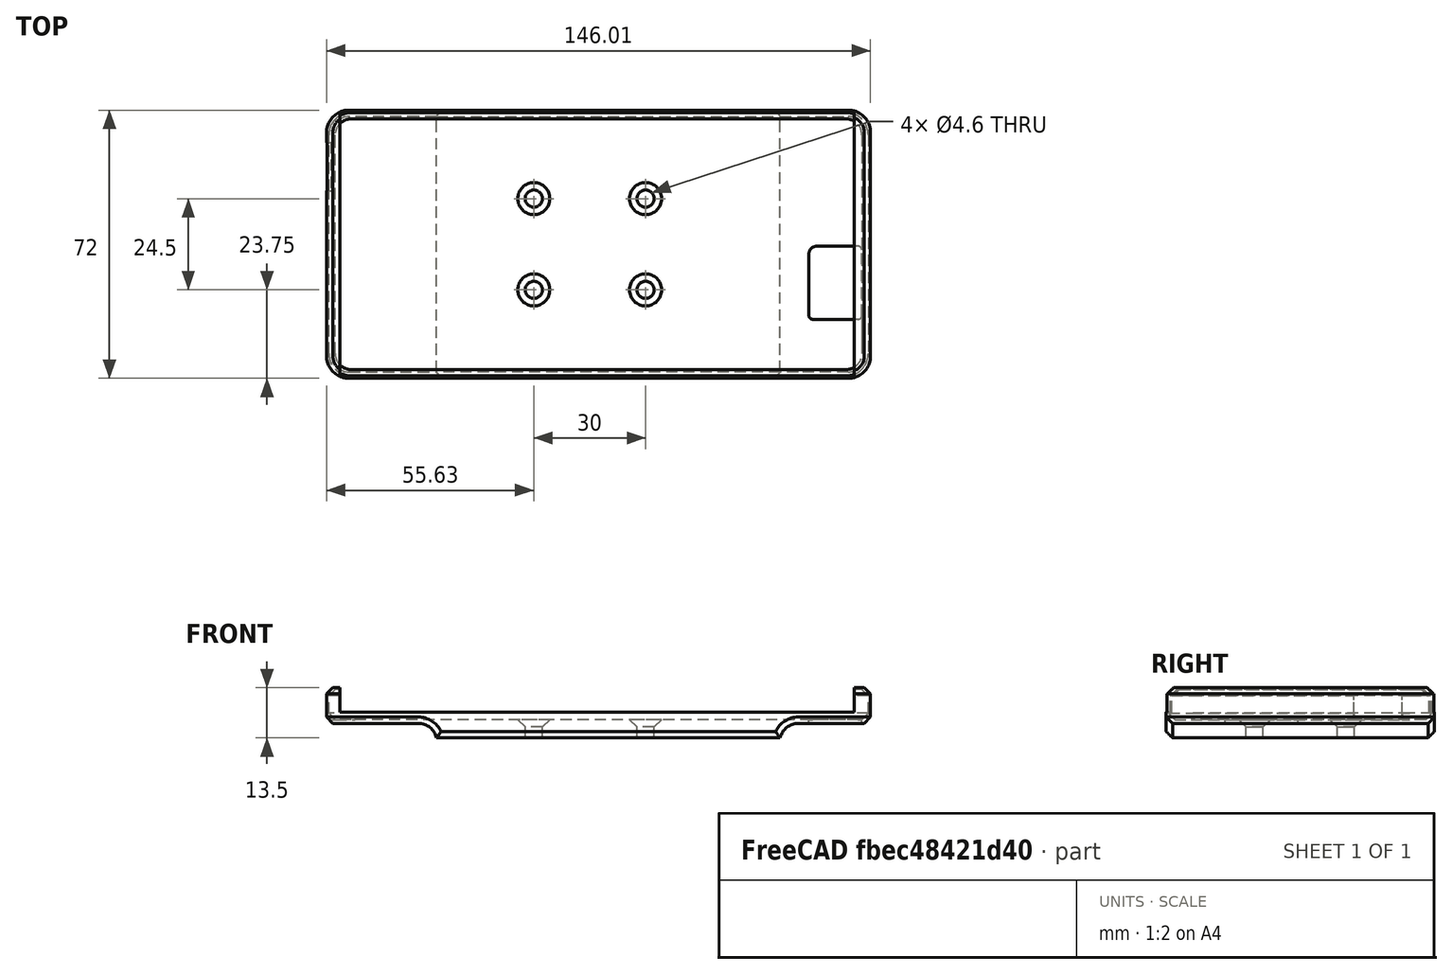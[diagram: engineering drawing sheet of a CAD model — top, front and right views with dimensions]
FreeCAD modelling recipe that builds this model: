
FCSTD DOCUMENT  (FreeCAD 0.16R5235 (Git))
Label: support_wiko_smart-roadster_i02
License: All rights reserved
LicenseURL: http://en.wikipedia.org/wiki/All_rights_reserved
objects: Part::Box×7, Part::Cut×7, Part::Fillet×5, Part::Chamfer×5, Part::Cylinder×4, Part::Fuse×3
note: 31 computed .brp shape members not serialized (recipe doc carries the construction recipe); baked Part::Feature solids carry a one-line shape summary decoded from their .brp

FEATURE [Part::Box] Box  label="Base_Highway_4G"
  Height = 8.1
  Length = 144.75
  Width = 70.7
FEATURE [Part::Box] Box001  label="Base_boitier"
  Height = 13.5
  Length = 146
  Placement = pos=(-0.625,-0.65,-4.9) rot=(0,0,1;0rad)
  Width = 72
FEATURE [Part::Fillet] Fillet  label="W_Rayon_6"
  Base = -> Box
  Edges = 4 edges r=6: [Edge1,Edge3,Edge5,Edge7]
FEATURE [Part::Fillet] Fillet001  label="B_Rayon_6"
  Base = -> Box001
  Edges = 4 edges r=6: [Edge1,Edge3,Edge5,Edge7]
FEATURE [Part::Chamfer] Chamfer  label="W_Chanf_1,7"
  Base = -> Fillet
  Edges = 2 edges r=1.7: [Edge1,Edge4]
FEATURE [Part::Cut] Cut  label="Boitier_trouée_wiko"
  Base = -> Fillet001
  Tool = -> Chamfer
FEATURE [Part::Box] Box002  label="Cube_trou_ouverture_supérieure"
  Height = 10
  Length = 138
  Placement = pos=(3,-4,2) rot=(0,0,1;0rad)
  Width = 80
FEATURE [Part::Cut] Cut001  label="Boitier_ouvert"
  Base = -> Cut
  Tool = -> Box002
FEATURE [Part::Chamfer] Chamfer001  label="Boitier_ouvert_chanf"
  Base = -> Cut001
  Edges = 3 edges r=1.7: [Edge1,Edge4,Edge48]
FEATURE [Part::Cylinder] Cylinder  label="Trou_fixation_1"
  Angle = 360
  Height = 15
  Placement = pos=(0,0,-7) rot=(0,0,1;0rad)
  Radius = 2.3
FEATURE [Part::Cylinder] Cylinder001  label="Trou_fixation_2"
  Angle = 360
  Height = 15
  Placement = pos=(0,24.5,-7) rot=(0,0,1;0rad)
  Radius = 2.3
FEATURE [Part::Cylinder] Cylinder002  label="Trou_fixation_3"
  Angle = 360
  Height = 15
  Placement = pos=(30,24.5,-7) rot=(0,0,1;0rad)
  Radius = 2.3
FEATURE [Part::Cylinder] Cylinder003  label="Trou_fixation_4"
  Angle = 360
  Height = 15
  Placement = pos=(30,0,-7) rot=(0,0,1;0rad)
  Radius = 2.3
FEATURE [Part::Fuse] Fusion
  Base = -> Cylinder
  Tool = -> Cylinder001
FEATURE [Part::Fuse] Fusion001
  Base = -> Fusion
  Tool = -> Cylinder002
FEATURE [Part::Fuse] Fusion002  label="Bloc_des_trous"
  Base = -> Fusion001
  Placement = pos=(55,23.1,0) rot=(0,0,1;0rad)
  Tool = -> Cylinder003
FEATURE [Part::Cut] Cut002  label="Boitier_percé_fix"
  Base = -> Chamfer001
  Tool = -> Fusion002
FEATURE [Part::Chamfer] Chamfer002  label="Boitier_percé_fix_chanf"
  Base = -> Cut002
  Edges = 4 edges r=2: [Edge99,Edge101,Edge103,Edge105]
FEATURE [Part::Box] Box003  label="Evidement_inf_1"
  Height = 10
  Length = 30
  Placement = pos=(-1,-6,-11) rot=(0,0,1;0rad)
  Width = 80
FEATURE [Part::Box] Box004  label="Evidement_inf_2"
  Height = 10
  Length = 55
  Placement = pos=(121,-6,-11) rot=(0,0,1;0rad)
  Width = 80
FEATURE [Part::Fillet] Fillet002  label="Evidement_inf_1_arrondi"
  Base = -> Box003
  Edges = 1 edges r=5: [Edge6]
FEATURE [Part::Fillet] Fillet003  label="Evidement_inf_2_arrondi"
  Base = -> Box004
  Edges = 1 edges r=5: [Edge2]
FEATURE [Part::Cut] Cut003
  Base = -> Chamfer002
  Tool = -> Fillet002
FEATURE [Part::Cut] Cut004  label="Boitier_évidé_inf"
  Base = -> Cut003
  Tool = -> Fillet003
FEATURE [Part::Chamfer] Chamfer003
  Base = -> Cut004
  Edges = 1 edges r=1.7: [Edge72]
FEATURE [Part::Chamfer] Chamfer004  label="Boitié_évidé_inf_chanf"
  Base = -> Chamfer003
  Edges = 1 edges r=1.7: [Edge75]
FEATURE [Part::Box] Box005  label="Trou_USB"
  Height = 7
  Length = 10
  Placement = pos=(-3,49.7,0) rot=(0,0,1;0rad)
  Width = 13
FEATURE [Part::Cut] Cut005  label="Boitier"
  Base = -> Chamfer004
  Tool = -> Box005
FEATURE [Part::Box] Box006  label="Trou_objectif_photo"
  Height = 10
  Length = 14.2
  Placement = pos=(128.85,15.2,-5) rot=(0,0,1;0rad)
  Width = 19.6
FEATURE [Part::Fillet] Fillet004  label="Trou_obj_photo_congés"
  Base = -> Box006
  Edges = 4 edges: [Edge1 r=1,Edge3 r=2,Edge5 r=1,Edge7 r=1]
FEATURE [Part::Cut] Cut006  label="Boitier_obj_photo"
  Base = -> Cut005
  Tool = -> Fillet004
